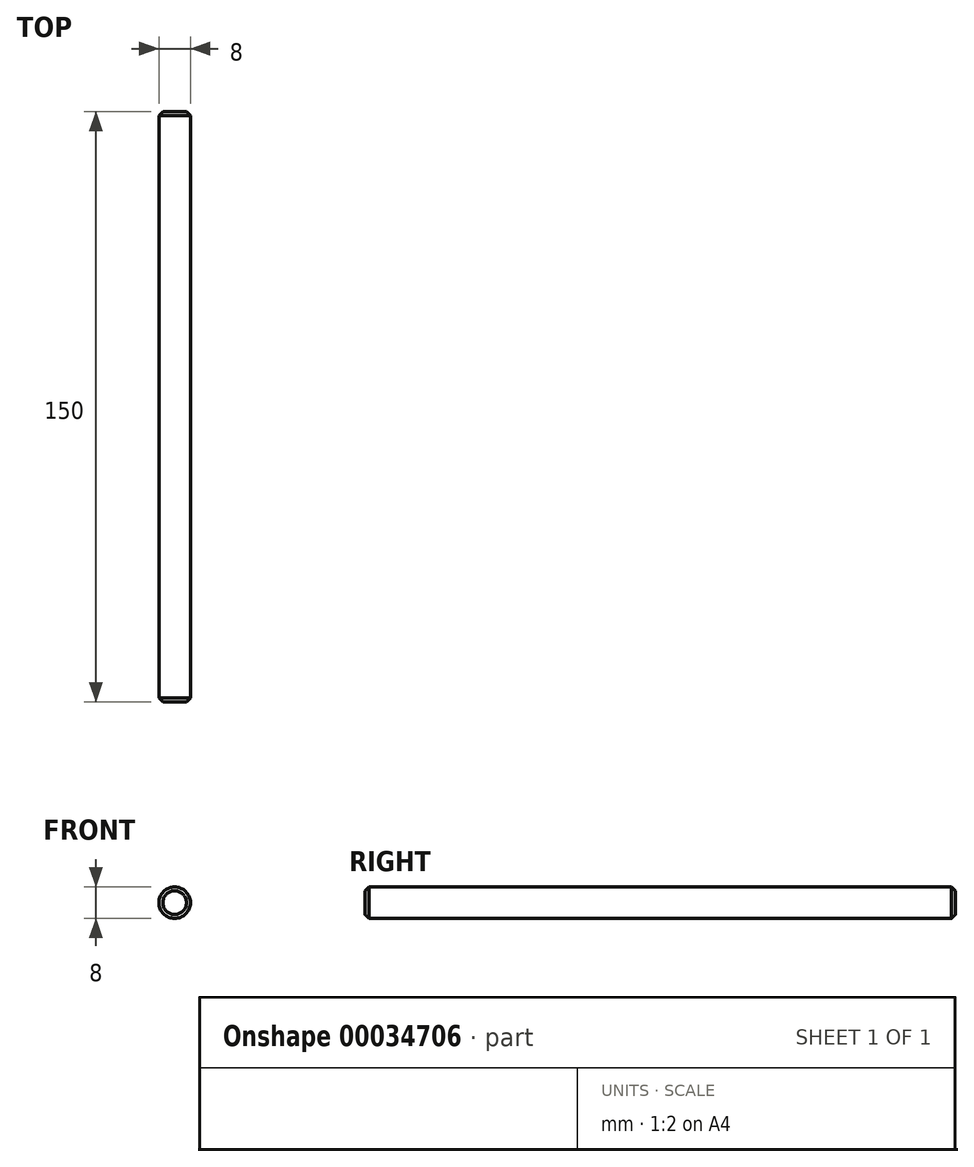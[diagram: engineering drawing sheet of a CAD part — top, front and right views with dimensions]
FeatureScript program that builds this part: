
annotation { "Feature Type Name" : "Feature", "Feature Type Description" : "" }
export const myFeature = defineFeature(function(context is Context, id is Id, definition is map)
    precondition{}
    {
        {
            var Q0;
            Q0=qCreatedBy(makeId("Front.planeOp"),FACE);
            var sketch = newSketch(context, id + "F0", { "sketchPlane" : qUnion([Q0])});
            skCircle(sketch, "E0", {"center": v(0, 0) * mm, "radius": 4 * mm});
            skSolve(sketch);
        }
        {
            var Q0;
            Q0=makeQuery(id+"F0.imprint","IMPRINT",FACE,{"disambiguationData":[TD([[makeQuery(id+"F0.imprint","IMPRINT",EDGE,{"derivedFrom":sQuery(id+"F0.wireOp",EDGE,"E0")}),1.0]])]});
            extrude(context, id + "F1", {"entities" : qUnion([Q0]), "depth" : 150 * mm});
        }
        {
            var Q0;
            Q0=makeQuery(id+"F1.opExtrude","CAP_EDGE",EDGE,{"disambiguationData":[OSD([sQuery(id+"F0.wireOp",EDGE,"E0")])],"isStart":true});
            var Q1;
            Q1=makeQuery(id+"F1.opExtrude","CAP_EDGE",EDGE,{"disambiguationData":[OSD([sQuery(id+"F0.wireOp",EDGE,"E0")])],"isStart":false});
            chamfer(context, id + "F2", {"entities" : qUnion([Q0, Q1]), "width" : 1 * mm, "tangentPropagation" : true});
        }
    });
